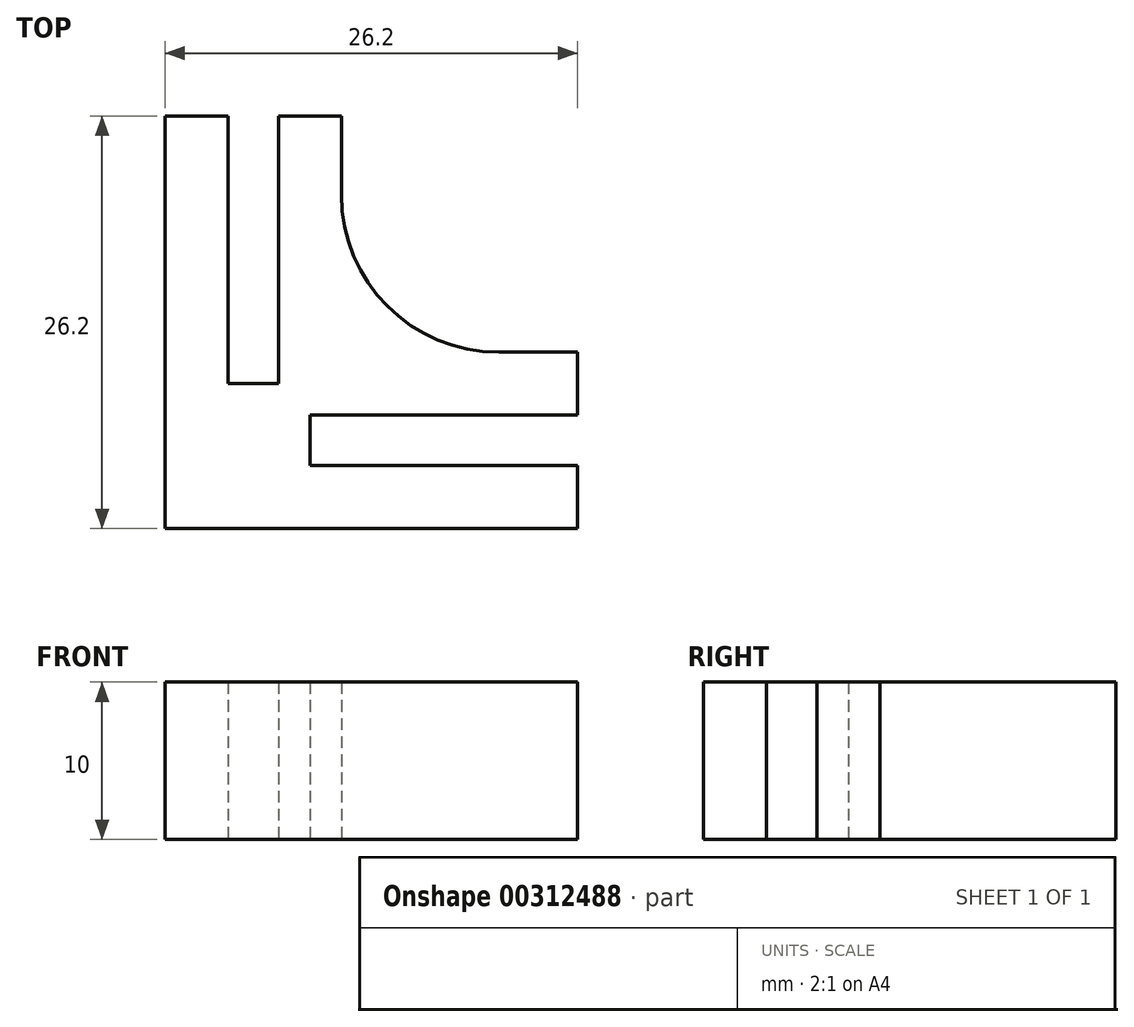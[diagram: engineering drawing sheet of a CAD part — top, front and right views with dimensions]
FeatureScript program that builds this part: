
annotation { "Feature Type Name" : "Feature", "Feature Type Description" : "" }
export const myFeature = defineFeature(function(context is Context, id is Id, definition is map)
    precondition{}
    {
        {
            assignVariable(context, id + "F0", {"name" : "d", "anyValue" : 10});
        }
        {
            var Q0;
            Q0=qCreatedBy(makeId("Top.planeOp"),FACE);
            var sketch = newSketch(context, id + "F1", { "sketchPlane" : qUnion([Q0])});
            skLineSegment(sketch, "E0", {"start": v(-2, 20.6) * mm, "end": v(-2, 3.6) * mm});
            skLineSegment(sketch, "E1", {"start": v(-2, 3.6) * mm, "end": v(-5.2, 3.6) * mm});
            skLineSegment(sketch, "E2", {"start": v(-5.2, 3.6) * mm, "end": v(-5.2, 20.6) * mm});
            skLineSegment(sketch, "E3", {"start": v(-5.2, 20.6) * mm, "end": v(-9.2, 20.6) * mm});
            skLineSegment(sketch, "E4", {"start": v(-9.2, 20.6) * mm, "end": v(-9.2, -5.6) * mm});
            skLineSegment(sketch, "E5", {"start": v(-9.2, -5.6) * mm, "end": v(17, -5.6) * mm});
            skLineSegment(sketch, "E6", {"start": v(17, -5.6) * mm, "end": v(17, -1.6) * mm});
            skLineSegment(sketch, "E7", {"start": v(17, -1.6) * mm, "end": v(0, -1.6) * mm});
            skLineSegment(sketch, "E8", {"start": v(0, -1.6) * mm, "end": v(0, 1.6) * mm});
            skLineSegment(sketch, "E9", {"start": v(0, 1.6) * mm, "end": v(17, 1.6) * mm});
            skLineSegment(sketch, "E10", {"start": v(17, 1.6) * mm, "end": v(17, 5.6) * mm});
            skLineSegment(sketch, "E11", {"start": v(17, 5.6) * mm, "end": v(2, 5.6) * mm});
            skLineSegment(sketch, "E12", {"start": v(2, 5.6) * mm, "end": v(2, 20.6) * mm});
            skLineSegment(sketch, "E13", {"start": v(2, 20.6) * mm, "end": v(-2, 20.6) * mm});
            skLineSegment(sketch, "E14", {"start": v(-2, 3.6) * mm, "end": v(0, 3.6) * mm, "construction": true});
            skLineSegment(sketch, "E15", {"start": v(0, 1.6) * mm, "end": v(0, 3.6) * mm, "construction": true});
            skPoint(sketch, "E16", {"position": v(0, 0) * mm});
            skSolve(sketch);
        }
        {
            var Q0;
            Q0=makeQuery(id+"F1.imprint","IMPRINT",FACE,{"disambiguationData":[TD([[makeQuery(id+"F1.imprint","IMPRINT",EDGE,{"derivedFrom":sQuery(id+"F1.wireOp",EDGE,"E0")}),1.0]])]});
            extrude(context, id + "F2", {"entities" : qUnion([Q0]), "depth" : (getVariable(context, 'd')) * mm});
        }
        {
            var Q0;
            Q0=makeQuery(id+"F2.opExtrude","SWEPT_EDGE",EDGE,{"disambiguationData":[OSD([sQuery(id+"F1.wireOp",EDGE,"E11"),sQuery(id+"F1.wireOp",EDGE,"E12")])]});
            fillet(context, id + "F3", {"entities" : qUnion([Q0]), "radius" : 10 * mm, "tangentPropagation" : true, "allowEdgeOverflow" : false});
        }
    });
